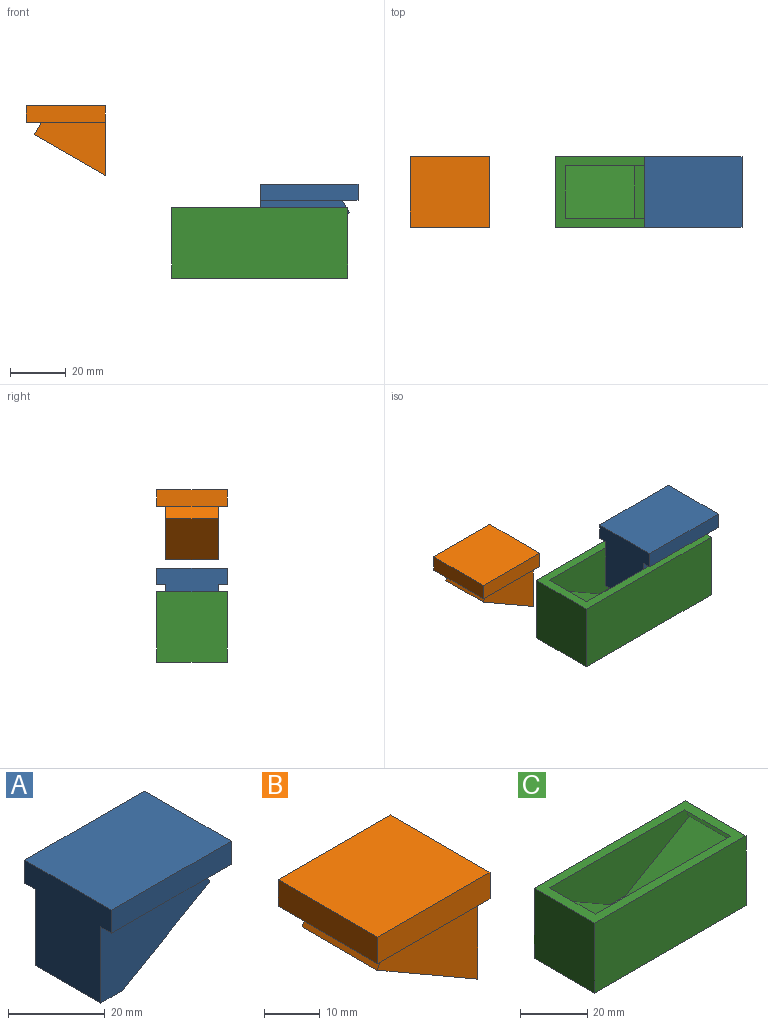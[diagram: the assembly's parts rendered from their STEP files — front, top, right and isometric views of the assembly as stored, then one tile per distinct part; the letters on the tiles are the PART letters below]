
ASSEMBLY  parts=3 mates=3
PART A: 11 faces, bbox 35x25.4x25.1 mm
  f0: plane 31.96x19.26mm, normal (0,1,0), area 420.6mm2, adj f2,f3,f4,f5,f6
  f1: plane 31.96x19.26mm, normal (0,-1,0), area 420.6mm2, adj f2,f3,f4,f5,f6
  f2: plane 25.4x25.11mm, normal (-1,0,0), area 515.4mm2, adj f0,f1,f3,f6,f8,f9,f10
  f3: plane 19.05x6.35mm, normal (0,0,-1), area 121mm2, adj f0,f1,f2,f4
  f4: plane 25.61x19.05mm, normal (0.5,0,-0.87), area 563.4mm2, adj f0,f1,f3,f5
  f5: plane 19.05x4.48mm, normal (0.87,0,0.5), area 98.5mm2, adj f0,f1,f4,f6
  f6: plane 35.02x25.4mm, normal (0,0,-1), area 329.8mm2, adj f0,f1,f2,f5,f7,f9,f10
  f7: plane 25.4x5.84mm, normal (1,0,0), area 148.4mm2, adj f6,f8,f9,f10
  f8: plane 35.02x25.4mm, normal (0,0,1), area 889.5mm2, adj f2,f7,f9,f10
  f9: plane 35.02x5.84mm, normal (0,-1,0), area 204.6mm2, adj f2,f6,f7,f8
  f10: plane 35.02x5.84mm, normal (0,1,0), area 204.6mm2, adj f2,f6,f7,f8
PART B: 10 faces, bbox 28.6x25.4x25.1 mm
  f0: plane 25.61x19.26mm, normal (0,1,0), area 298.2mm2, adj f2,f5,f6,f7
  f1: plane 25.61x19.26mm, normal (0,-1,0), area 298.2mm2, adj f2,f5,f6,f7
  f2: plane 25.4x25.11mm, normal (1,0,0), area 515.4mm2, adj f0,f1,f3,f5,f7,f8,f9
  f3: plane 28.58x25.4mm, normal (0,0,1), area 725.8mm2, adj f2,f4,f8,f9
  f4: plane 25.4x5.84mm, normal (-1,0,0), area 148.4mm2, adj f3,f5,f8,f9
  f5: plane 28.58x25.4mm, normal (0,0,-1), area 287.1mm2, adj f0,f1,f2,f4,f6,f8,f9
  f6: plane 19.05x4.48mm, normal (-0.87,0,0.5), area 98.5mm2, adj f0,f1,f5,f7
  f7: plane 25.61x19.05mm, normal (-0.5,0,-0.87), area 563.4mm2, adj f0,f1,f2,f6
  f8: plane 28.58x5.84mm, normal (0,-1,0), area 166.9mm2, adj f2,f3,f4,f5
  f9: plane 28.58x5.84mm, normal (0,1,0), area 166.9mm2, adj f2,f3,f4,f5
PART C: 13 faces, bbox 63.5x25.4x25.4 mm
  f0: plane 26.99x19.05mm, normal (0.5,0,0.87), area 593.6mm2, adj f1,f8,f9,f11
  f1: plane 19.05x3.18mm, normal (0.87,0,-0.5), area 69.8mm2, adj f0,f5,f9,f11
  f2: plane 25.4x25.4mm, normal (-1,0,0), area 645.2mm2, adj f3,f5,f10,f12
  f3: plane 63.5x25.4mm, normal (0,0,-1), area 1612.9mm2, adj f2,f4,f10,f12
  f4: plane 25.4x25.4mm, normal (1,0,0), area 645.2mm2, adj f3,f5,f10,f12
  f5: plane 63.5x25.4mm, normal (0,0,1), area 533.5mm2, adj f1,f2,f4,f6,f9,f10,f11,f12
  f6: plane 19.05x3.18mm, normal (-0.87,0,-0.5), area 69.8mm2, adj f5,f7,f9,f11
  f7: plane 26.99x19.05mm, normal (-0.5,0,0.87), area 593.6mm2, adj f6,f8,f9,f11
  f8: plane 19.05x6.35mm, normal (0,0,1), area 121mm2, adj f0,f7,f9,f11
  f9: plane 60.33x18.76mm, normal (0,1,0), area 705.2mm2, adj f0,f1,f5,f6,f7,f8
  f10: plane 63.5x25.4mm, normal (0,-1,0), area 1612.9mm2, adj f2,f3,f4,f5
  f11: plane 60.33x18.76mm, normal (0,-1,0), area 705.2mm2, adj f0,f1,f5,f6,f7,f8
  f12: plane 63.5x25.4mm, normal (0,1,0), area 1612.9mm2, adj f2,f3,f4,f5
PLACE A t=(23.25,-15.12,-11.64)mm
PLACE B t=(-32.72,-15.12,16.58)mm
PLACE C t=(19.7,-15.12,-13.69)mm
MATE planar C.f7 <-> A.f4  axis (-0.5,0,0.87) through (36.37,-15.12,-11.96)mm
MATE planar C.f7 <-> A.f4  axis (-0.5,0,0.87) through (36.37,-15.12,-11.96)mm
MATE planar B.f7 <-> C.f0  axis (-0.5,0,-0.87) through (-48.7,-15.12,17.91)mm
